# Revit family: Durawatt Mini Dual Unit With Stand
name_source: partatom
category: Generic Models
units: mm (PartAtom-declared; Revit-internal decimal feet)

## family parameters
Always vertical = Yes
Can host rebar = No
Cut with Voids When Loaded = No
Maintain Annotation Orientation = No
Part Type = Normal
Room Calculation Point = No
Round Connector Dimension = Use Diameter
Shared = No
Work Plane-Based = No

## types (1)
- Standard
    Cold Inlet (Lower Unit) - NPT = 0' - 1 1/2"
    Cold Inlet (Upper Unit)- NPT = 0' - 1 1/2"
    Default Elevation = 0' - 0"
    Description = Durawatt® Mini is a compact, high-performance electric water heater
    Hot Outlet (Lower Unit) - NPT = 0' - 1 1/2"
    Hot Outlet (Upper Unit) - NPT = 0' - 1 1/2"
    Manufacturer = PVI
    Model = Durawatt® Mini (Dual Stacked)
    Relief Valve (Lower Unit) - NPT = 0' - 0 3/4"
    Relief Valve (Upper Unit) - NPT = 0' - 0 3/4"
    URL = www.pvi.com

## geometry (parser evidence)
native form markers: Sweep x3
no freeform markers — native parametric forms only
